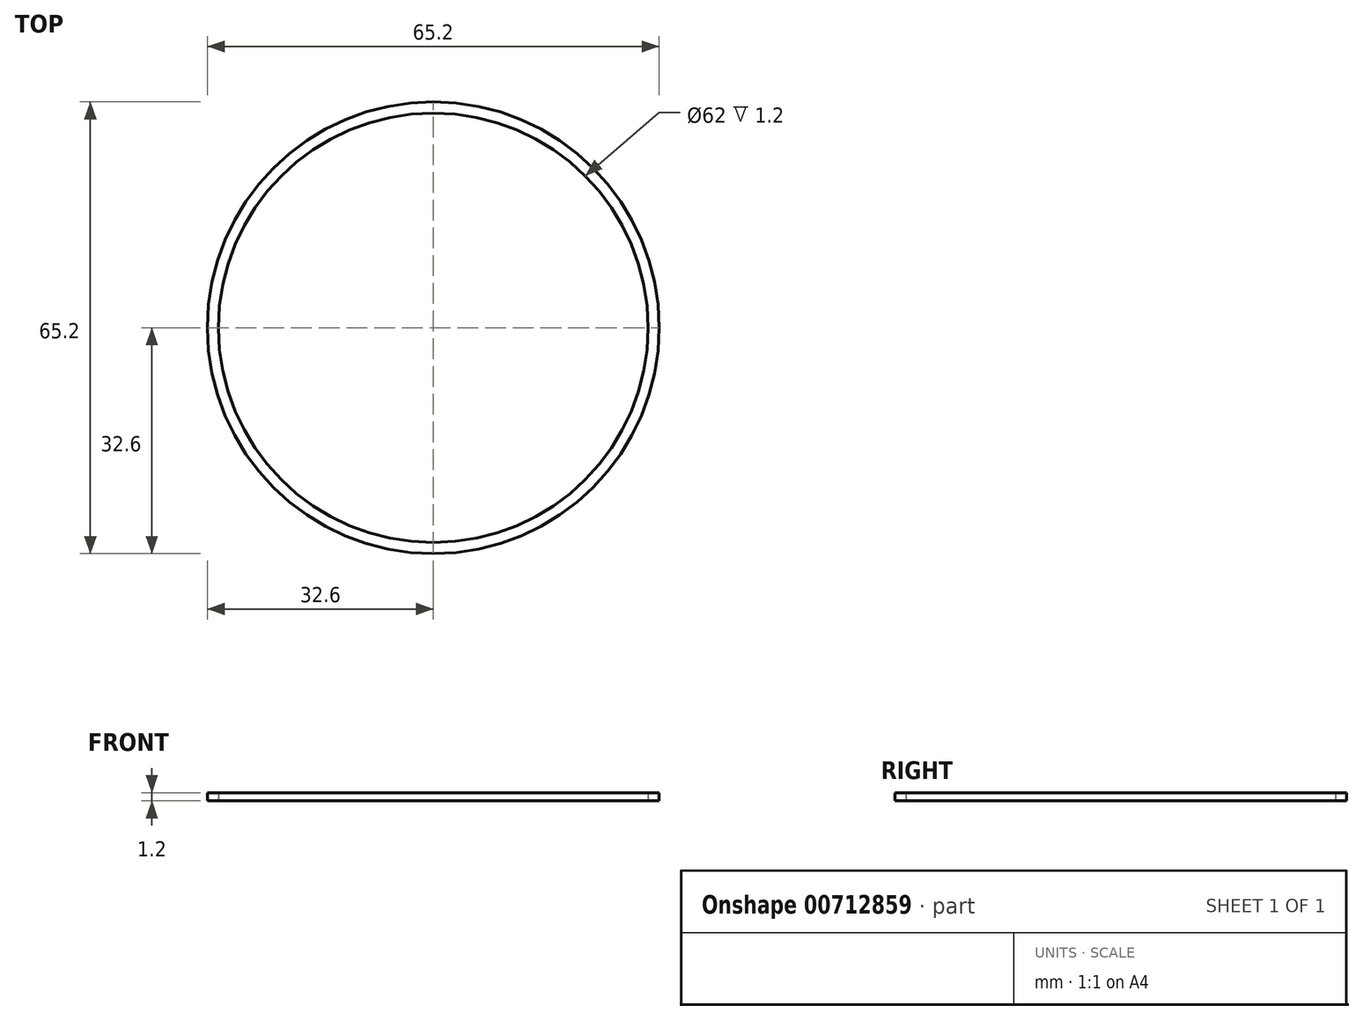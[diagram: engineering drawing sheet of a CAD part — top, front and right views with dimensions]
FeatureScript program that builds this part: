
annotation { "Feature Type Name" : "Feature", "Feature Type Description" : "" }
export const myFeature = defineFeature(function(context is Context, id is Id, definition is map)
    precondition{}
    {
        {
            var Q0;
            Q0=qCreatedBy(makeId("Top.planeOp"),FACE);
            var sketch = newSketch(context, id + "F0", { "sketchPlane" : qUnion([Q0])});
            skCircle(sketch, "E0", {"center": v(0, 0) * mm, "radius": 31 * mm});
            skCircle(sketch, "E1.0", {"center": v(0, 0) * mm, "radius": 32.6 * mm});
            skSolve(sketch);
        }
        {
            var Q0;
            Q0 = qSketchRegion(id + "F0", true);
            extrude(context, id + "F1", {"entities" : qUnion([Q0]), "depth" : 1.2 * mm, "offsetDistance" : 25 * mm});
        }
    });
